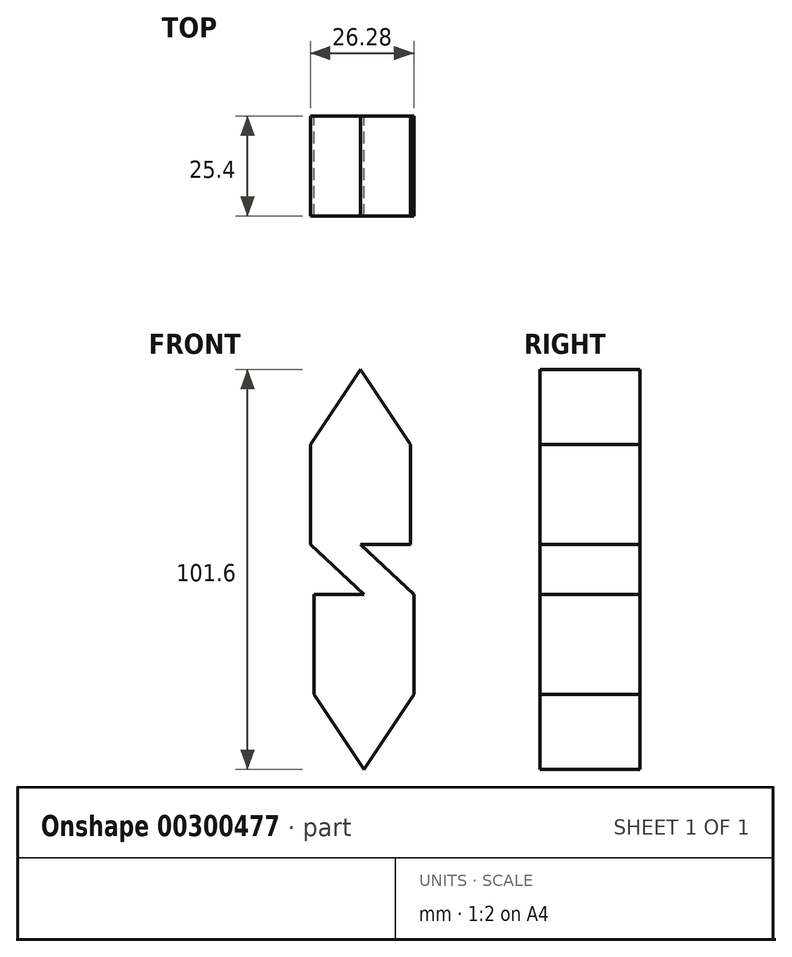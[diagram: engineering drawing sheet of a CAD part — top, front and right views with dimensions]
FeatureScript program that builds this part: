
annotation { "Feature Type Name" : "Feature", "Feature Type Description" : "" }
export const myFeature = defineFeature(function(context is Context, id is Id, definition is map)
    precondition{}
    {
        {
            var Q0;
            Q0=qCreatedBy(makeId("Front.planeOp"),FACE);
            var sketch = newSketch(context, id + "F0", { "sketchPlane" : qUnion([Q0])});
            skLineSegment(sketch, "E0", {"start": v(-38.18, 30.4) * mm, "end": v(-38.18, 5) * mm});
            skLineSegment(sketch, "E1", {"start": v(-12.78, 30.4) * mm, "end": v(-12.78, 5) * mm});
            skLineSegment(sketch, "E2", {"start": v(-11.9, -7.7) * mm, "end": v(-11.9, -33.1) * mm});
            skLineSegment(sketch, "E3", {"start": v(-37.3, -7.7) * mm, "end": v(-37.3, -33.1) * mm});
            skPoint(sketch, "E4", {"position": v(-25.48, 49.44) * mm});
            skLineSegment(sketch, "E5", {"start": v(-38.18, 30.4) * mm, "end": v(-25.48, 49.44) * mm});
            skLineSegment(sketch, "E6", {"start": v(-25.48, 49.44) * mm, "end": v(-12.78, 30.4) * mm});
            skPoint(sketch, "E7", {"position": v(-24.6, -52.16) * mm});
            skLineSegment(sketch, "E8", {"start": v(-24.6, -52.16) * mm, "end": v(-37.3, -33.1) * mm});
            skLineSegment(sketch, "E9", {"start": v(-24.6, -52.16) * mm, "end": v(-11.9, -33.1) * mm});
            skLineSegment(sketch, "E10", {"start": v(-38.18, 5) * mm, "end": v(-24.6, -7.7) * mm});
            skLineSegment(sketch, "E11", {"start": v(-11.9, -7.7) * mm, "end": v(-25.48, 5) * mm});
            skLineSegment(sketch, "E12", {"start": v(-37.3, -7.7) * mm, "end": v(-24.6, -7.7) * mm});
            skLineSegment(sketch, "E13", {"start": v(-12.78, 5) * mm, "end": v(-25.48, 5) * mm});
            skPoint(sketch, "E14", {"position": v(-25.79, 30.53) * mm});
            skPoint(sketch, "E15", {"position": v(-32.04, 10.24) * mm});
            skPoint(sketch, "E16", {"position": v(-18.2, 11.56) * mm});
            skPoint(sketch, "E17", {"position": v(-25.03, -33) * mm});
            skPoint(sketch, "E18", {"position": v(-32.8, -14.22) * mm});
            skPoint(sketch, "E19", {"position": v(-18.2, -14.22) * mm});
            skLineSegment(sketch, "E20", {"start": v(-32.04, 10.24) * mm, "end": v(-25.79, 30.53) * mm});
            skLineSegment(sketch, "E21", {"start": v(-25.79, 30.53) * mm, "end": v(-18.2, 11.56) * mm});
            skSolve(sketch);
        }
        {
            var Q0;
            Q0=makeQuery(id+"F0.imprint","IMPRINT",FACE,{"disambiguationData":[TD([[makeQuery(id+"F0.imprint","IMPRINT",EDGE,{"derivedFrom":sQuery(id+"F0.wireOp",EDGE,"E0")}),1.0]])]});
            extrude(context, id + "F1", {"entities" : qUnion([Q0]), "depth" : 25.4 * mm});
        }
    });
